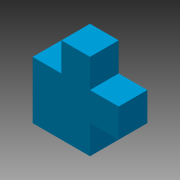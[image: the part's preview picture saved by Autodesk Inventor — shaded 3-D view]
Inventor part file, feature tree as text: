
AUTODESK INVENTOR PART (.ipt)
format: ipt  version: 2015 (Build 190159000, 159)  size: 87,552 bytes
history: native  units: in
note: dims shown in document units (in); Inventor stores cm internally (conversion verified against a paired STEP export)
features: extrude x1, sketch x1
ambient origin geometry x8: Origin, YZ Plane, XZ Plane, XY Plane, X Axis, Y Axis, Z Axis, Center Point
bodies: Solid1 (feature_tree)
feature tree (2):
  extrude  "Extrusion1"  Depth=0.75in
  sketch  "Sketch1"  dims[d0=1.5in d1=0.75in d2=0.75in d3=0.75in d4=0.75in d5=0.75in d6=0.75in d7=0.75in d8=0.75in d9=0.0in]
